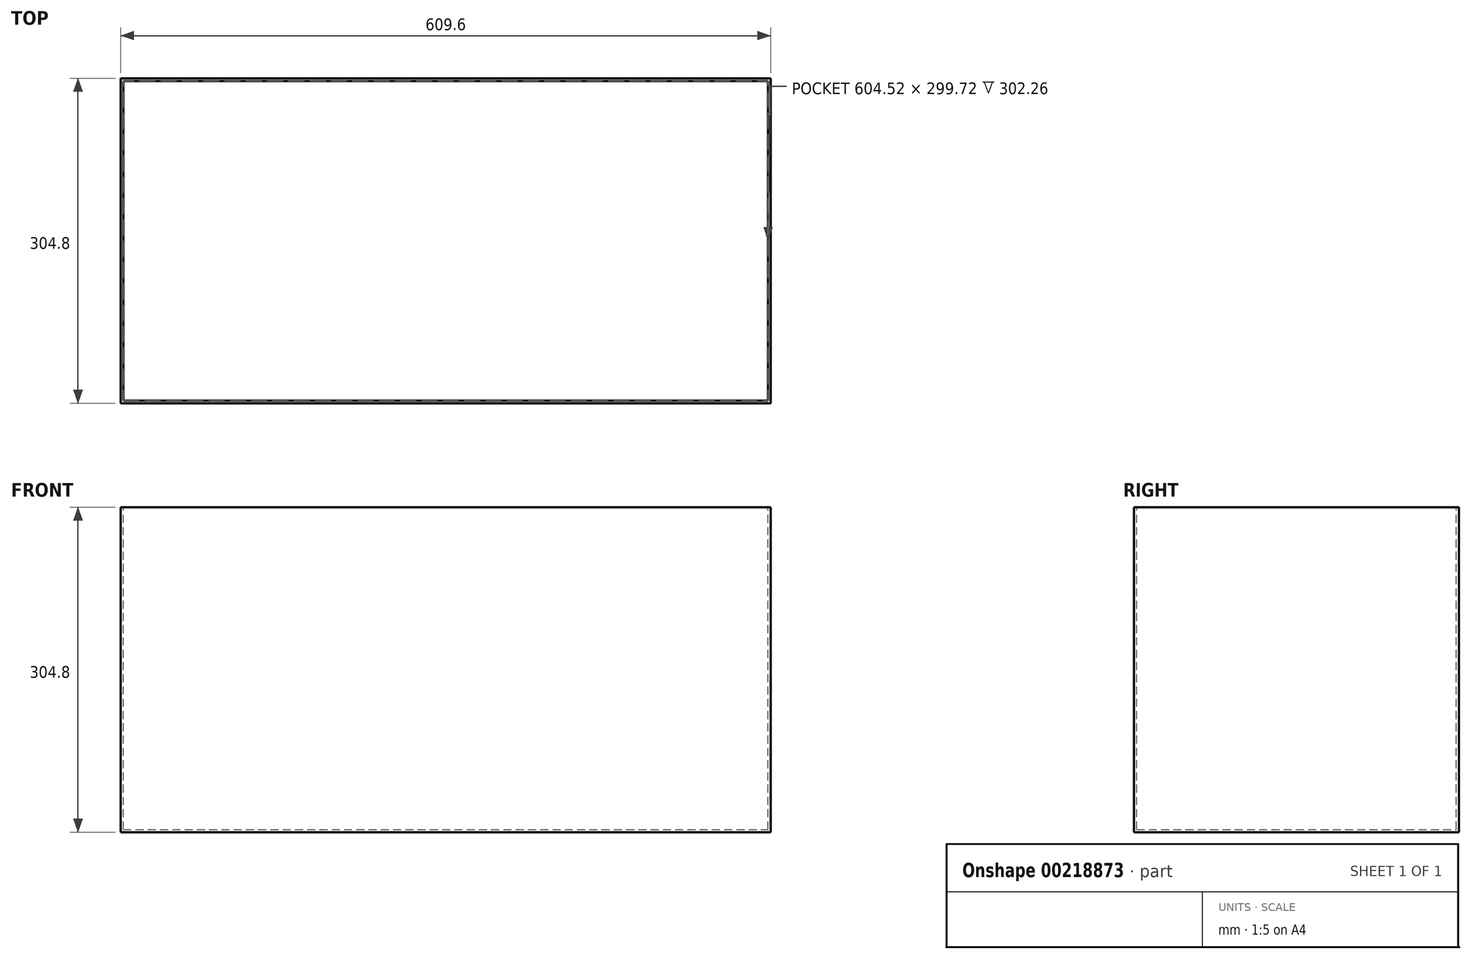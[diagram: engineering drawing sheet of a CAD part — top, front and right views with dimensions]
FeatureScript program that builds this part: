
annotation { "Feature Type Name" : "Feature", "Feature Type Description" : "" }
export const myFeature = defineFeature(function(context is Context, id is Id, definition is map)
    precondition{}
    {
        {
            var Q0;
            Q0=qCreatedBy(makeId("Top.planeOp"),FACE);
            var sketch = newSketch(context, id + "F0", { "sketchPlane" : qUnion([Q0])});
            skLineSegment(sketch, "E0.bottom", {"start": v(304.8, -152.4) * mm, "end": v(-304.8, -152.4) * mm});
            skLineSegment(sketch, "E0.top", {"start": v(304.8, 152.4) * mm, "end": v(-304.8, 152.4) * mm});
            skLineSegment(sketch, "E0.left", {"start": v(304.8, -152.4) * mm, "end": v(304.8, 152.4) * mm});
            skLineSegment(sketch, "E0.right", {"start": v(-304.8, -152.4) * mm, "end": v(-304.8, 152.4) * mm});
            skPoint(sketch, "E0.middle", {"position": v(0, 0) * mm});
            skSolve(sketch);
        }
        {
            var Q0;
            Q0 = qSketchRegion(id + "F0", true);
            extrude(context, id + "F1", {"entities" : qUnion([Q0]), "depth" : 304.8 * mm});
        }
        {
            var Q0;
            Q0=makeQuery(id+"F1.opExtrude","CAP_FACE",FACE,{"disambiguationData":[OSD([sQuery(id+"F0.wireOp",EDGE,"E0.bottom"),sQuery(id+"F0.wireOp",EDGE,"E0.top"),sQuery(id+"F0.wireOp",EDGE,"E0.left"),sQuery(id+"F0.wireOp",EDGE,"E0.right")])],"isStart":false});
            var sketch = newSketch(context, id + "F2", { "sketchPlane" : qUnion([Q0])});
            skLineSegment(sketch, "E1.0", {"start": v(302.26, -149.86) * mm, "end": v(302.26, 149.86) * mm});
            skLineSegment(sketch, "E1.1", {"start": v(-302.26, -149.86) * mm, "end": v(302.26, -149.86) * mm});
            skLineSegment(sketch, "E1.2", {"start": v(-302.26, 149.86) * mm, "end": v(-302.26, -149.86) * mm});
            skLineSegment(sketch, "E1.3", {"start": v(302.26, 149.86) * mm, "end": v(-302.26, 149.86) * mm});
            skSolve(sketch);
        }
        {
            var Q0;
            Q0 = qSketchRegion(id + "F2", true);
            extrude(context, id + "F3", {"entities" : qUnion([Q0]), "operationType" : NewBodyOperationType.REMOVE, "oppositeDirection" : true, "depth" : 302.26 * mm});
        }
    });
